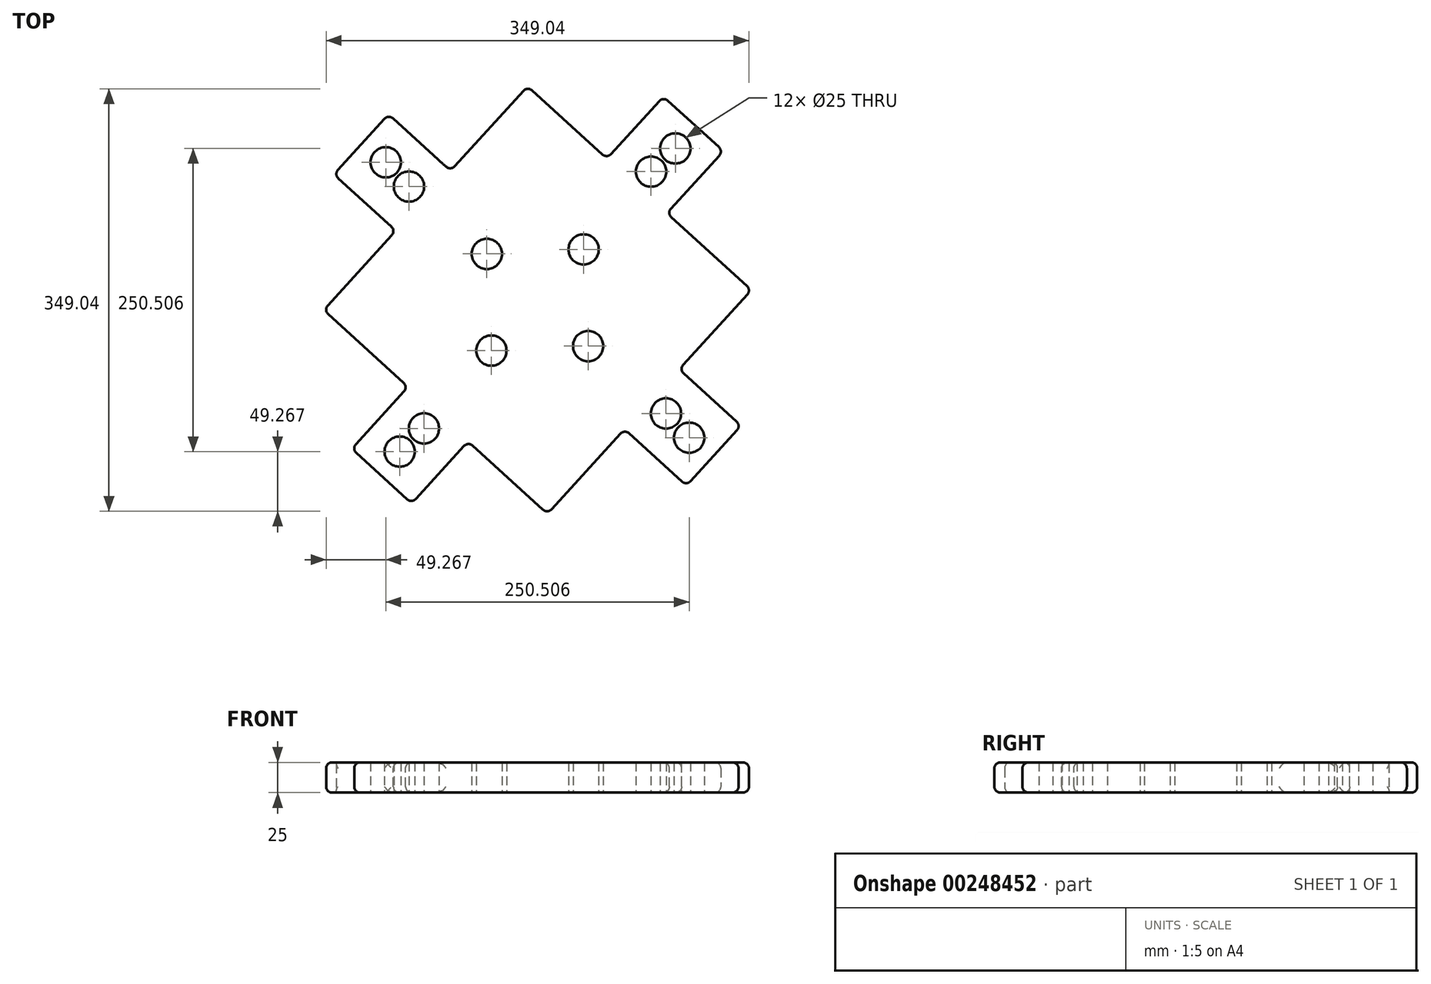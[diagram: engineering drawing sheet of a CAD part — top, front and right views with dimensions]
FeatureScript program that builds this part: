
annotation { "Feature Type Name" : "Feature", "Feature Type Description" : "" }
export const myFeature = defineFeature(function(context is Context, id is Id, definition is map)
    precondition{}
    {
        {
            var Q0;
            Q0=qCreatedBy(makeId("Top.planeOp"),FACE);
            var sketch = newSketch(context, id + "F0", { "sketchPlane" : qUnion([Q0])});
            skCircle(sketch, "E0", {"center": v(0, 0) * mm, "radius": 125 * mm});
            skCircle(sketch, "E1.cCircle", {"center": v(0, 0) * mm, "radius": 125 * mm, "construction": true});
            skLineSegment(sketch, "E1.0", {"start": v(-8.24, 176.58) * mm, "end": v(176.58, 8.24) * mm});
            skLineSegment(sketch, "E1.1", {"start": v(176.58, 8.24) * mm, "end": v(8.24, -176.58) * mm});
            skLineSegment(sketch, "E1.2", {"start": v(8.24, -176.58) * mm, "end": v(-176.58, -8.24) * mm});
            skLineSegment(sketch, "E1.3", {"start": v(-176.58, -8.24) * mm, "end": v(-8.24, 176.58) * mm});
            skPoint(sketch, "E1.0.midPoint", {"position": v(84.17, 92.41) * mm});
            skLineSegment(sketch, "E2", {"start": v(57.27, 116.91) * mm, "end": v(103.88, 168.08) * mm});
            skLineSegment(sketch, "E3", {"start": v(103.88, 168.08) * mm, "end": v(153.4, 122.97) * mm});
            skLineSegment(sketch, "E4", {"start": v(153.4, 122.97) * mm, "end": v(106.8, 71.8) * mm});
            skLineSegment(sketch, "E5", {"start": v(0, 0) * mm, "end": v(-112.8, 102.74) * mm});
            skLineSegment(sketch, "E6", {"start": v(0, 0) * mm, "end": v(-61.22, -67.2) * mm});
            skLineSegment(sketch, "E7.1.0", {"start": v(-116.91, 57.27) * mm, "end": v(-168.08, 103.88) * mm});
            skLineSegment(sketch, "E7.1.1", {"start": v(-168.08, 103.88) * mm, "end": v(-122.97, 153.4) * mm});
            skLineSegment(sketch, "E7.1.2", {"start": v(-122.97, 153.4) * mm, "end": v(-71.8, 106.8) * mm});
            skLineSegment(sketch, "E7.2.0", {"start": v(-57.27, -116.91) * mm, "end": v(-103.88, -168.08) * mm});
            skLineSegment(sketch, "E7.2.1", {"start": v(-103.88, -168.08) * mm, "end": v(-153.4, -122.97) * mm});
            skLineSegment(sketch, "E7.2.2", {"start": v(-153.4, -122.97) * mm, "end": v(-106.8, -71.8) * mm});
            skLineSegment(sketch, "E7.3.0", {"start": v(116.91, -57.27) * mm, "end": v(168.08, -103.88) * mm});
            skLineSegment(sketch, "E7.3.1", {"start": v(168.08, -103.88) * mm, "end": v(122.97, -153.4) * mm});
            skLineSegment(sketch, "E7.3.2", {"start": v(122.97, -153.4) * mm, "end": v(71.8, -106.8) * mm});
            skCircle(sketch, "E8", {"center": v(-113.77, -125.25) * mm, "radius": 12.5 * mm});
            skCircle(sketch, "E9", {"center": v(-93.75, -106.09) * mm, "radius": 12.5 * mm});
            skCircle(sketch, "E10.1.0", {"center": v(125.25, -113.77) * mm, "radius": 12.5 * mm});
            skCircle(sketch, "E10.1.1", {"center": v(106.09, -93.75) * mm, "radius": 12.5 * mm});
            skCircle(sketch, "E10.2.0", {"center": v(113.77, 125.25) * mm, "radius": 12.5 * mm});
            skCircle(sketch, "E10.2.1", {"center": v(93.75, 106.09) * mm, "radius": 12.5 * mm});
            skCircle(sketch, "E10.3.0", {"center": v(-125.25, 113.77) * mm, "radius": 12.5 * mm});
            skCircle(sketch, "E10.3.1", {"center": v(-106.09, 93.75) * mm, "radius": 12.5 * mm});
            skCircle(sketch, "E11", {"center": v(-41.8, 38.08) * mm, "radius": 12.5 * mm});
            skCircle(sketch, "E12.1.0", {"center": v(-38.08, -41.8) * mm, "radius": 12.5 * mm});
            skCircle(sketch, "E12.2.0", {"center": v(41.8, -38.08) * mm, "radius": 12.5 * mm});
            skCircle(sketch, "E12.3.0", {"center": v(38.08, 41.8) * mm, "radius": 12.5 * mm});
            skSolve(sketch);
        }
        {
            var Q0;
            Q0 = qSketchRegion(id + "F0", true);
            var Q1;
            {var subQ0=sQuery(id+"F0.wireOp",EDGE,"E0");var subQ1=makeQuery(id+"F0.imprint","INTERSECT",VERTEX,{"derivedFrom":[subQ0,sQuery(id+"F0.wireOp",EDGE,"E1.3")]});Q1=makeQuery(id+"F0.imprint","IMPRINT",FACE,{"disambiguationData":[TD([[makeQuery(id+"F0.imprint","IMPRINT",EDGE,{"disambiguationData":[TD([[subQ1,1.0]])],"derivedFrom":subQ0}),1.0]])]});}
            extrude(context, id + "F1", {"entities" : qUnion([Q0, Q1]), "depth" : 25 * mm});
        }
        {
            var Q0;
            {var subQ0=sQuery(id+"F0.wireOp",EDGE,"E1.3");Q0=makeQuery(id+"F1.opExtrude","SWEPT_FACE",FACE,{"disambiguationData":[OSD([subQ0]),TDD([makeQuery(id+"F0.imprint","IMPRINT",EDGE,{"disambiguationData":[TD([[makeQuery(id+"F0.imprint","INTERSECT",VERTEX,{"derivedFrom":[sQuery(id+"F0.wireOp",EDGE,"E1.0"),subQ0]}),1.0]])],"derivedFrom":subQ0})])]});}
            var Q1;
            {var subQ0=sQuery(id+"F0.wireOp",EDGE,"E1.0");Q1=makeQuery(id+"F1.opExtrude","SWEPT_FACE",FACE,{"disambiguationData":[OSD([subQ0]),TDD([makeQuery(id+"F0.imprint","IMPRINT",EDGE,{"disambiguationData":[TD([[makeQuery(id+"F0.imprint","INTERSECT",VERTEX,{"derivedFrom":[subQ0,sQuery(id+"F0.wireOp",EDGE,"E1.3")]}),-1.0]])],"derivedFrom":subQ0})])]});}
            var Q2;
            Q2=makeQuery(id+"F1.opExtrude","SWEPT_FACE",FACE,{"disambiguationData":[OSD([sQuery(id+"F0.wireOp",EDGE,"E2")])]});
            var Q3;
            Q3=makeQuery(id+"F1.opExtrude","SWEPT_FACE",FACE,{"disambiguationData":[OSD([sQuery(id+"F0.wireOp",EDGE,"E7.1.1")])]});
            var Q4;
            Q4=makeQuery(id+"F1.opExtrude","SWEPT_FACE",FACE,{"disambiguationData":[OSD([sQuery(id+"F0.wireOp",EDGE,"E3")])]});
            var Q5;
            Q5=makeQuery(id+"F1.opExtrude","SWEPT_FACE",FACE,{"disambiguationData":[OSD([sQuery(id+"F0.wireOp",EDGE,"E4")])]});
            var Q6;
            {var subQ0=sQuery(id+"F0.wireOp",EDGE,"E1.1");Q6=makeQuery(id+"F1.opExtrude","SWEPT_FACE",FACE,{"disambiguationData":[OSD([subQ0]),TDD([makeQuery(id+"F0.imprint","IMPRINT",EDGE,{"disambiguationData":[TD([[makeQuery(id+"F0.imprint","INTERSECT",VERTEX,{"derivedFrom":[sQuery(id+"F0.wireOp",EDGE,"E1.0"),subQ0]}),-1.0]])],"derivedFrom":subQ0})])]});}
            var Q7;
            {var subQ0=sQuery(id+"F0.wireOp",EDGE,"E1.0");Q7=makeQuery(id+"F1.opExtrude","SWEPT_FACE",FACE,{"disambiguationData":[OSD([subQ0]),TDD([makeQuery(id+"F0.imprint","IMPRINT",EDGE,{"disambiguationData":[TD([[makeQuery(id+"F0.imprint","INTERSECT",VERTEX,{"derivedFrom":[subQ0,sQuery(id+"F0.wireOp",EDGE,"E1.1")]}),1.0]])],"derivedFrom":subQ0})])]});}
            var Q8;
            Q8=makeQuery(id+"F1.opExtrude","SWEPT_FACE",FACE,{"disambiguationData":[OSD([sQuery(id+"F0.wireOp",EDGE,"E7.3.0")])]});
            var Q9;
            Q9=makeQuery(id+"F1.opExtrude","SWEPT_FACE",FACE,{"disambiguationData":[OSD([sQuery(id+"F0.wireOp",EDGE,"E7.3.1")])]});
            var Q10;
            {var subQ0=sQuery(id+"F0.wireOp",EDGE,"E1.1");Q10=makeQuery(id+"F1.opExtrude","SWEPT_FACE",FACE,{"disambiguationData":[OSD([subQ0]),TDD([makeQuery(id+"F0.imprint","IMPRINT",EDGE,{"disambiguationData":[TD([[makeQuery(id+"F0.imprint","INTERSECT",VERTEX,{"derivedFrom":[subQ0,sQuery(id+"F0.wireOp",EDGE,"E1.2")]}),1.0]])],"derivedFrom":subQ0})])]});}
            var Q11;
            Q11=makeQuery(id+"F1.opExtrude","SWEPT_FACE",FACE,{"disambiguationData":[OSD([sQuery(id+"F0.wireOp",EDGE,"E7.3.2")])]});
            var Q12;
            {var subQ0=sQuery(id+"F0.wireOp",EDGE,"E1.2");Q12=makeQuery(id+"F1.opExtrude","SWEPT_FACE",FACE,{"disambiguationData":[OSD([subQ0]),TDD([makeQuery(id+"F0.imprint","IMPRINT",EDGE,{"disambiguationData":[TD([[makeQuery(id+"F0.imprint","INTERSECT",VERTEX,{"derivedFrom":[sQuery(id+"F0.wireOp",EDGE,"E1.1"),subQ0]}),-1.0]])],"derivedFrom":subQ0})])]});}
            var Q13;
            Q13=makeQuery(id+"F1.opExtrude","SWEPT_FACE",FACE,{"disambiguationData":[OSD([sQuery(id+"F0.wireOp",EDGE,"E7.2.0")])]});
            var Q14;
            Q14=makeQuery(id+"F1.opExtrude","SWEPT_FACE",FACE,{"disambiguationData":[OSD([sQuery(id+"F0.wireOp",EDGE,"E7.2.1")])]});
            var Q15;
            Q15=makeQuery(id+"F1.opExtrude","SWEPT_FACE",FACE,{"disambiguationData":[OSD([sQuery(id+"F0.wireOp",EDGE,"E7.2.2")])]});
            var Q16;
            {var subQ0=sQuery(id+"F0.wireOp",EDGE,"E1.2");Q16=makeQuery(id+"F1.opExtrude","SWEPT_FACE",FACE,{"disambiguationData":[OSD([subQ0]),TDD([makeQuery(id+"F0.imprint","IMPRINT",EDGE,{"disambiguationData":[TD([[makeQuery(id+"F0.imprint","INTERSECT",VERTEX,{"derivedFrom":[subQ0,sQuery(id+"F0.wireOp",EDGE,"E1.3")]}),1.0]])],"derivedFrom":subQ0})])]});}
            var Q17;
            {var subQ0=sQuery(id+"F0.wireOp",EDGE,"E1.3");Q17=makeQuery(id+"F1.opExtrude","SWEPT_FACE",FACE,{"disambiguationData":[OSD([subQ0]),TDD([makeQuery(id+"F0.imprint","IMPRINT",EDGE,{"disambiguationData":[TD([[makeQuery(id+"F0.imprint","INTERSECT",VERTEX,{"derivedFrom":[sQuery(id+"F0.wireOp",EDGE,"E1.2"),subQ0]}),-1.0]])],"derivedFrom":subQ0})])]});}
            fillet(context, id + "F2", {"entities" : qUnion([Q0, Q1, Q2, Q3, Q4, Q5, Q6, Q7, Q8, Q9, Q10, Q11, Q12, Q13, Q14, Q15, Q16, Q17]), "radius" : 5 * mm, "tangentPropagation" : true, "allowEdgeOverflow" : false});
        }
    });
